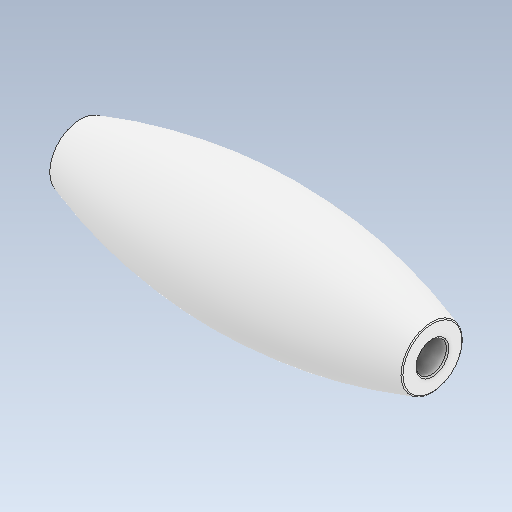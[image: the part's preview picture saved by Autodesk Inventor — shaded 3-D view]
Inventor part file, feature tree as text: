
AUTODESK INVENTOR PART (.ipt)
format: ipt  version: 2020.2 (Build 242310000, 310)  size: 124,928 bytes
history: native  units: in
note: dims shown in document units (in); Inventor stores cm internally (conversion verified against a paired STEP export)
features: fillet x1
ambient origin geometry x8: Origin, YZ Plane, XZ Plane, XY Plane, X Axis, Y Axis, Z Axis, Center Point
bodies: Solid1 (feature_tree)
feature tree (1):
  fillet  "Fillet1"  [1 undecoded]
note: 1 required parameter value undecoded (feature->parameter linkage not recoverable at this tier; creation-order binding heuristic only, values carry confidence <= 0.55)
